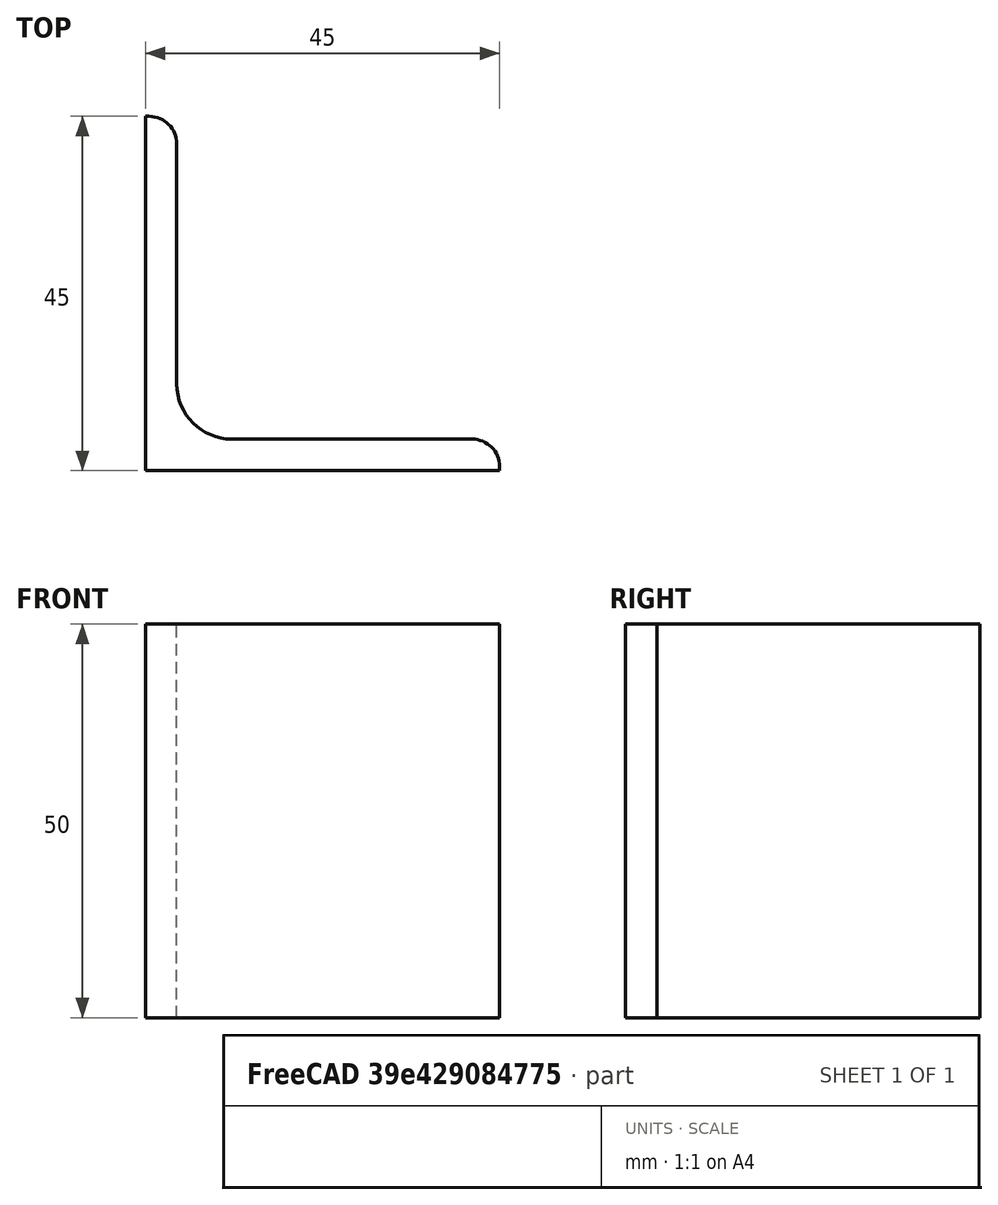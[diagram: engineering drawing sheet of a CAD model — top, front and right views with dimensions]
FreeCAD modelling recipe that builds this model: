
FCSTD DOCUMENT  (FreeCAD 0.15R4671 (Git))
Label: Angle Bar L45x45x4 EN10056 S235JR
License: All rights reserved
LicenseURL: http://en.wikipedia.org/wiki/All_rights_reserved
objects: Sketcher::SketchObject×1, Part::Extrusion×1
note: 2 computed .brp shape members not serialized (recipe doc carries the construction recipe); baked Part::Feature solids carry a one-line shape summary decoded from their .brp

FEATURE [Sketcher::SketchObject] Sketch
  sketch-geometry (9):
    g0: LineSegment StartX=0 StartY=0 StartZ=0 EndX=45 EndY=0 EndZ=0
    g1: LineSegment StartX=45 StartY=0 StartZ=0 EndX=45 EndY=0.5 EndZ=0
    g2: LineSegment StartX=41.5 StartY=4 StartZ=0 EndX=11 EndY=4 EndZ=0
    g3: LineSegment StartX=0 StartY=0 StartZ=0 EndX=0 EndY=45 EndZ=0
    g4: LineSegment StartX=0 StartY=45 StartZ=0 EndX=0.5 EndY=45 EndZ=0
    g5: LineSegment StartX=4 StartY=41.5 StartZ=0 EndX=4 EndY=11 EndZ=0
    g6: ArcOfCircle CenterX=11 CenterY=11 CenterZ=0 NormalX=0 NormalY=0 NormalZ=1 Radius=7 StartAngle=3.14159 EndAngle=4.71239
    g7: ArcOfCircle CenterX=0.5 CenterY=41.5 CenterZ=0 NormalX=0 NormalY=0 NormalZ=1 Radius=3.5 StartAngle=0 EndAngle=1.5708
    g8: ArcOfCircle CenterX=41.5 CenterY=0.5 CenterZ=0 NormalX=0 NormalY=0 NormalZ=1 Radius=3.5 StartAngle=0 EndAngle=1.5708
  constraints (23):
    c: Coincident(g0,g-1)
    c: Horizontal(g0)
    c: Coincident(g1,g0)
    c: Vertical(g1)
    c: Horizontal(g2)
    c: Coincident(g3,g-1)
    c: Vertical(g3)
    c: Coincident(g4,g3)
    c: Horizontal(g4)
    c: Vertical(g5)
    c: Tangent(g5,g6) = -1.5708
    c: Tangent(g2,g6) = 1.5708
    c: Tangent(g4,g7) = 1.5708
    c: Tangent(g5,g7) = 1.5708
    c: Tangent(g2,g8) = -1.5708
    c: Tangent(g1,g8) = -1.5708
    c: DistanceX(g0) = 45
    c: DistanceY(g3) = 45
    c: DistanceY(g0,g2) = 4
    c: DistanceX(g3,g5) = 4
    c: Radius(g6) = 7
    c: Radius(g8) = 3.5
    c: Radius(g7) = 3.5
FEATURE [Part::Extrusion] Extrude  label="Angle Bar L45x45x4 EN10056 S235JR"
  Base = -> Sketch
  Dir = (0,0,50)
  Solid = true
